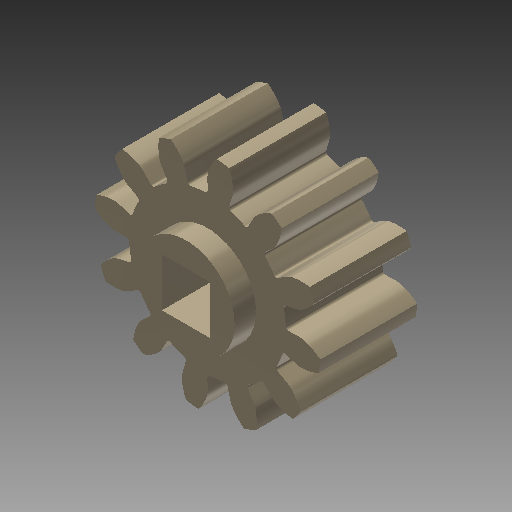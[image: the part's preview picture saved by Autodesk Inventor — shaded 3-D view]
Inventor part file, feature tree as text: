
AUTODESK INVENTOR PART (.ipt)
format: ipt  version: 2018 (Build 220112000, 112)  size: 508,416 bytes
history: native  units: mm (DEFAULTED — no unit token found)
features: imported_body x1, sketch x1, other x1, extrude x1
ambient origin geometry x8: Origin, YZ Plane, XZ Plane, XY Plane, X Axis, Y Axis, Z Axis, Center Point
bodies: Solid1 (feature_tree)
feature tree (4):
  imported_body  "Base1"
  sketch  "Sketch2"  dims[d1=6.35mm d3=25.4mm d4=0.0mm d5=0.0mm d6=0.0mm]
  other  "Srf1"
  extrude  "ExtrusionSrf1"  Depth=25.4mm TaperAngle=0.0deg
